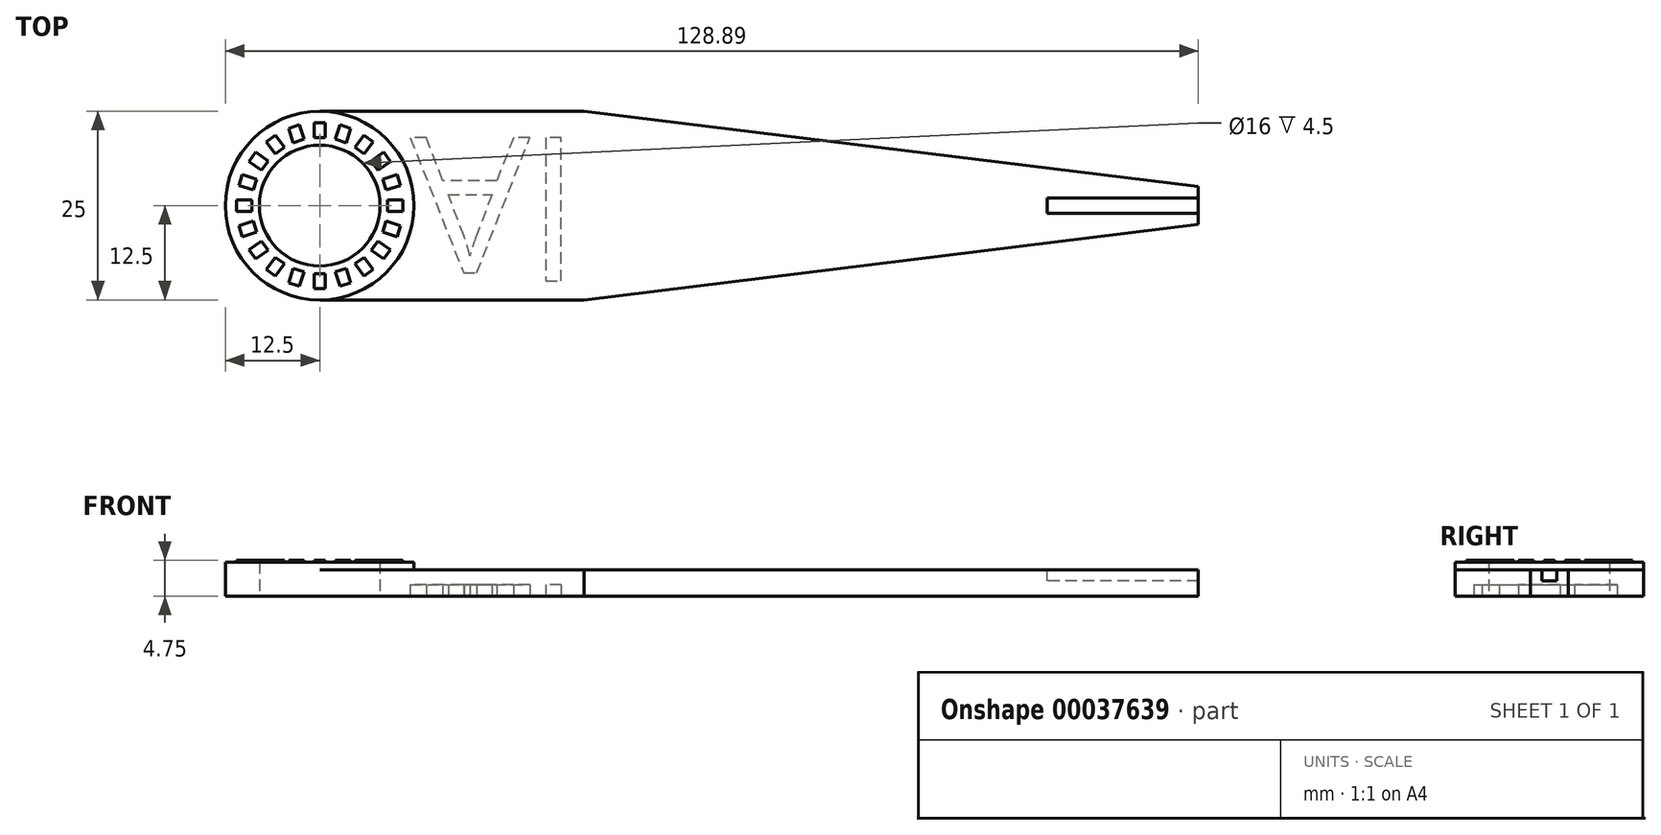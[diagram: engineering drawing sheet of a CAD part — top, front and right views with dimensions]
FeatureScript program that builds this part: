
annotation { "Feature Type Name" : "Feature", "Feature Type Description" : "" }
export const myFeature = defineFeature(function(context is Context, id is Id, definition is map)
    precondition{}
    {
        {
            var Q0;
            Q0=qCreatedBy(makeId("Top.planeOp"),FACE);
            var sketch = newSketch(context, id + "F0", { "sketchPlane" : qUnion([Q0])});
            skCircle(sketch, "E0", {"center": v(0, 0) * mm, "radius": 8 * mm});
            skCircle(sketch, "E1", {"center": v(0, 0) * mm, "radius": 12.5 * mm});
            skLineSegment(sketch, "E2", {"start": v(0, 12.5) * mm, "end": v(35, 12.5) * mm});
            skPoint(sketch, "E3", {"position": v(0, 12.5) * mm});
            skLineSegment(sketch, "E4", {"start": v(35, 12.5) * mm, "end": v(64.7, 12.5) * mm, "construction": true});
            skLineSegment(sketch, "E5", {"start": v(35, 12.5) * mm, "end": v(116.39, 2.5) * mm});
            skLineSegment(sketch, "E6", {"start": v(0, 0) * mm, "end": v(42.98, 0) * mm, "construction": true});
            skLineSegment(sketch, "E7.MirrorCS", {"start": v(35, -12.5) * mm, "end": v(116.39, -2.5) * mm});
            skLineSegment(sketch, "E8", {"start": v(116.39, 2.5) * mm, "end": v(116.39, -2.5) * mm});
            skLineSegment(sketch, "E9.MirrorCS", {"start": v(0, -12.5) * mm, "end": v(35, -12.5) * mm});
            skSolve(sketch);
        }
        {
            var Q0;
            Q0 = qSketchRegion(id + "F0", true);
            extrude(context, id + "F1", {"entities" : qUnion([Q0]), "depth" : 3.5 * mm});
        }
        {
            var Q0;
            Q0=makeQuery(id+"F1.opExtrude","CAP_FACE",FACE,{"disambiguationData":[OSD([sQuery(id+"F0.wireOp",EDGE,"E0"),sQuery(id+"F0.wireOp",EDGE,"E1"),sQuery(id+"F0.wireOp",EDGE,"E2"),sQuery(id+"F0.wireOp",EDGE,"E5"),sQuery(id+"F0.wireOp",EDGE,"E7.MirrorCS"),sQuery(id+"F0.wireOp",EDGE,"E8"),sQuery(id+"F0.wireOp",EDGE,"E9.MirrorCS")])],"isStart":false});
            var sketch = newSketch(context, id + "F2", { "sketchPlane" : qUnion([Q0])});
            skCircle(sketch, "E10", {"center": v(0, 0) * mm, "radius": 8 * mm});
            skCircle(sketch, "E11", {"center": v(0, 0) * mm, "radius": 12.5 * mm});
            skSolve(sketch);
        }
        {
            var Q0;
            Q0 = qSketchRegion(id + "F2", true);
            extrude(context, id + "F3", {"entities" : qUnion([Q0]), "operationType" : NewBodyOperationType.ADD, "depth" : 1 * mm});
        }
        {
            var Q0;
            Q0=makeQuery(id+"F3.opExtrude","CAP_FACE",FACE,{"disambiguationData":[OSD([sQuery(id+"F2.wireOp",EDGE,"E10"),sQuery(id+"F2.wireOp",EDGE,"E11")])],"isStart":false});
            var sketch = newSketch(context, id + "F4", { "sketchPlane" : qUnion([Q0])});
            skLineSegment(sketch, "E12.bottom", {"start": v(-0.75, 11) * mm, "end": v(0.75, 11) * mm});
            skLineSegment(sketch, "E12.top", {"start": v(-0.75, 9) * mm, "end": v(0.75, 9) * mm});
            skLineSegment(sketch, "E12.left", {"start": v(-0.75, 11) * mm, "end": v(-0.75, 9) * mm});
            skLineSegment(sketch, "E12.right", {"start": v(0.75, 11) * mm, "end": v(0.75, 9) * mm});
            skPoint(sketch, "E13", {"position": v(0, 8) * mm});
            skLineSegment(sketch, "E14.1.0", {"start": v(-4.11, 10.23) * mm, "end": v(-2.69, 10.7) * mm});
            skLineSegment(sketch, "E14.1.1", {"start": v(-4.11, 10.23) * mm, "end": v(-3.5, 8.33) * mm});
            skLineSegment(sketch, "E14.1.2", {"start": v(-3.5, 8.33) * mm, "end": v(-2.07, 8.8) * mm});
            skLineSegment(sketch, "E14.1.3", {"start": v(-2.69, 10.7) * mm, "end": v(-2.07, 8.8) * mm});
            skLineSegment(sketch, "E14.2.0", {"start": v(-7.07, 8.46) * mm, "end": v(-5.86, 9.34) * mm});
            skLineSegment(sketch, "E14.2.1", {"start": v(-7.07, 8.46) * mm, "end": v(-5.9, 6.84) * mm});
            skLineSegment(sketch, "E14.2.2", {"start": v(-5.9, 6.84) * mm, "end": v(-4.68, 7.72) * mm});
            skLineSegment(sketch, "E14.2.3", {"start": v(-5.86, 9.34) * mm, "end": v(-4.68, 7.72) * mm});
            skLineSegment(sketch, "E14.3.0", {"start": v(-9.34, 5.86) * mm, "end": v(-8.46, 7.07) * mm});
            skLineSegment(sketch, "E14.3.1", {"start": v(-9.34, 5.86) * mm, "end": v(-7.72, 4.68) * mm});
            skLineSegment(sketch, "E14.3.2", {"start": v(-7.72, 4.68) * mm, "end": v(-6.84, 5.9) * mm});
            skLineSegment(sketch, "E14.3.3", {"start": v(-8.46, 7.07) * mm, "end": v(-6.84, 5.9) * mm});
            skLineSegment(sketch, "E14.4.0", {"start": v(-10.7, 2.69) * mm, "end": v(-10.23, 4.11) * mm});
            skLineSegment(sketch, "E14.4.1", {"start": v(-10.7, 2.69) * mm, "end": v(-8.8, 2.07) * mm});
            skLineSegment(sketch, "E14.4.2", {"start": v(-8.8, 2.07) * mm, "end": v(-8.33, 3.5) * mm});
            skLineSegment(sketch, "E14.4.3", {"start": v(-10.23, 4.11) * mm, "end": v(-8.33, 3.5) * mm});
            skLineSegment(sketch, "E14.5.0", {"start": v(-11, -0.75) * mm, "end": v(-11, 0.75) * mm});
            skLineSegment(sketch, "E14.5.1", {"start": v(-11, -0.75) * mm, "end": v(-9, -0.75) * mm});
            skLineSegment(sketch, "E14.5.2", {"start": v(-9, -0.75) * mm, "end": v(-9, 0.75) * mm});
            skLineSegment(sketch, "E14.5.3", {"start": v(-11, 0.75) * mm, "end": v(-9, 0.75) * mm});
            skLineSegment(sketch, "E14.6.0", {"start": v(-10.23, -4.11) * mm, "end": v(-10.7, -2.69) * mm});
            skLineSegment(sketch, "E14.6.1", {"start": v(-10.23, -4.11) * mm, "end": v(-8.33, -3.5) * mm});
            skLineSegment(sketch, "E14.6.2", {"start": v(-8.33, -3.5) * mm, "end": v(-8.8, -2.07) * mm});
            skLineSegment(sketch, "E14.6.3", {"start": v(-10.7, -2.69) * mm, "end": v(-8.8, -2.07) * mm});
            skLineSegment(sketch, "E14.7.0", {"start": v(-8.46, -7.07) * mm, "end": v(-9.34, -5.86) * mm});
            skLineSegment(sketch, "E14.7.1", {"start": v(-8.46, -7.07) * mm, "end": v(-6.84, -5.9) * mm});
            skLineSegment(sketch, "E14.7.2", {"start": v(-6.84, -5.9) * mm, "end": v(-7.72, -4.68) * mm});
            skLineSegment(sketch, "E14.7.3", {"start": v(-9.34, -5.86) * mm, "end": v(-7.72, -4.68) * mm});
            skLineSegment(sketch, "E14.8.0", {"start": v(-5.86, -9.34) * mm, "end": v(-7.07, -8.46) * mm});
            skLineSegment(sketch, "E14.8.1", {"start": v(-5.86, -9.34) * mm, "end": v(-4.68, -7.72) * mm});
            skLineSegment(sketch, "E14.8.2", {"start": v(-4.68, -7.72) * mm, "end": v(-5.9, -6.84) * mm});
            skLineSegment(sketch, "E14.8.3", {"start": v(-7.07, -8.46) * mm, "end": v(-5.9, -6.84) * mm});
            skLineSegment(sketch, "E14.9.0", {"start": v(-2.69, -10.7) * mm, "end": v(-4.11, -10.23) * mm});
            skLineSegment(sketch, "E14.9.1", {"start": v(-2.69, -10.7) * mm, "end": v(-2.07, -8.8) * mm});
            skLineSegment(sketch, "E14.9.2", {"start": v(-2.07, -8.8) * mm, "end": v(-3.5, -8.33) * mm});
            skLineSegment(sketch, "E14.9.3", {"start": v(-4.11, -10.23) * mm, "end": v(-3.5, -8.33) * mm});
            skLineSegment(sketch, "E14.10.0", {"start": v(0.75, -11) * mm, "end": v(-0.75, -11) * mm});
            skLineSegment(sketch, "E14.10.1", {"start": v(0.75, -11) * mm, "end": v(0.75, -9) * mm});
            skLineSegment(sketch, "E14.10.2", {"start": v(0.75, -9) * mm, "end": v(-0.75, -9) * mm});
            skLineSegment(sketch, "E14.10.3", {"start": v(-0.75, -11) * mm, "end": v(-0.75, -9) * mm});
            skLineSegment(sketch, "E14.11.0", {"start": v(4.11, -10.23) * mm, "end": v(2.69, -10.7) * mm});
            skLineSegment(sketch, "E14.11.1", {"start": v(4.11, -10.23) * mm, "end": v(3.5, -8.33) * mm});
            skLineSegment(sketch, "E14.11.2", {"start": v(3.5, -8.33) * mm, "end": v(2.07, -8.8) * mm});
            skLineSegment(sketch, "E14.11.3", {"start": v(2.69, -10.7) * mm, "end": v(2.07, -8.8) * mm});
            skLineSegment(sketch, "E14.12.0", {"start": v(7.07, -8.46) * mm, "end": v(5.86, -9.34) * mm});
            skLineSegment(sketch, "E14.12.1", {"start": v(7.07, -8.46) * mm, "end": v(5.9, -6.84) * mm});
            skLineSegment(sketch, "E14.12.2", {"start": v(5.9, -6.84) * mm, "end": v(4.68, -7.72) * mm});
            skLineSegment(sketch, "E14.12.3", {"start": v(5.86, -9.34) * mm, "end": v(4.68, -7.72) * mm});
            skLineSegment(sketch, "E14.13.0", {"start": v(9.34, -5.86) * mm, "end": v(8.46, -7.07) * mm});
            skLineSegment(sketch, "E14.13.1", {"start": v(9.34, -5.86) * mm, "end": v(7.72, -4.68) * mm});
            skLineSegment(sketch, "E14.13.2", {"start": v(7.72, -4.68) * mm, "end": v(6.84, -5.9) * mm});
            skLineSegment(sketch, "E14.13.3", {"start": v(8.46, -7.07) * mm, "end": v(6.84, -5.9) * mm});
            skLineSegment(sketch, "E14.14.0", {"start": v(10.7, -2.69) * mm, "end": v(10.23, -4.11) * mm});
            skLineSegment(sketch, "E14.14.1", {"start": v(10.7, -2.69) * mm, "end": v(8.8, -2.07) * mm});
            skLineSegment(sketch, "E14.14.2", {"start": v(8.8, -2.07) * mm, "end": v(8.33, -3.5) * mm});
            skLineSegment(sketch, "E14.14.3", {"start": v(10.23, -4.11) * mm, "end": v(8.33, -3.5) * mm});
            skLineSegment(sketch, "E14.15.0", {"start": v(11, 0.75) * mm, "end": v(11, -0.75) * mm});
            skLineSegment(sketch, "E14.15.1", {"start": v(11, 0.75) * mm, "end": v(9, 0.75) * mm});
            skLineSegment(sketch, "E14.15.2", {"start": v(9, 0.75) * mm, "end": v(9, -0.75) * mm});
            skLineSegment(sketch, "E14.15.3", {"start": v(11, -0.75) * mm, "end": v(9, -0.75) * mm});
            skLineSegment(sketch, "E14.16.0", {"start": v(10.23, 4.11) * mm, "end": v(10.7, 2.69) * mm});
            skLineSegment(sketch, "E14.16.1", {"start": v(10.23, 4.11) * mm, "end": v(8.33, 3.5) * mm});
            skLineSegment(sketch, "E14.16.2", {"start": v(8.33, 3.5) * mm, "end": v(8.8, 2.07) * mm});
            skLineSegment(sketch, "E14.16.3", {"start": v(10.7, 2.69) * mm, "end": v(8.8, 2.07) * mm});
            skLineSegment(sketch, "E14.17.0", {"start": v(8.46, 7.07) * mm, "end": v(9.34, 5.86) * mm});
            skLineSegment(sketch, "E14.17.1", {"start": v(8.46, 7.07) * mm, "end": v(6.84, 5.9) * mm});
            skLineSegment(sketch, "E14.17.2", {"start": v(6.84, 5.9) * mm, "end": v(7.72, 4.68) * mm});
            skLineSegment(sketch, "E14.17.3", {"start": v(9.34, 5.86) * mm, "end": v(7.72, 4.68) * mm});
            skLineSegment(sketch, "E14.18.0", {"start": v(5.86, 9.34) * mm, "end": v(7.07, 8.46) * mm});
            skLineSegment(sketch, "E14.18.1", {"start": v(5.86, 9.34) * mm, "end": v(4.68, 7.72) * mm});
            skLineSegment(sketch, "E14.18.2", {"start": v(4.68, 7.72) * mm, "end": v(5.9, 6.84) * mm});
            skLineSegment(sketch, "E14.18.3", {"start": v(7.07, 8.46) * mm, "end": v(5.9, 6.84) * mm});
            skLineSegment(sketch, "E14.19.0", {"start": v(2.69, 10.7) * mm, "end": v(4.11, 10.23) * mm});
            skLineSegment(sketch, "E14.19.1", {"start": v(2.69, 10.7) * mm, "end": v(2.07, 8.8) * mm});
            skLineSegment(sketch, "E14.19.2", {"start": v(2.07, 8.8) * mm, "end": v(3.5, 8.33) * mm});
            skLineSegment(sketch, "E14.19.3", {"start": v(4.11, 10.23) * mm, "end": v(3.5, 8.33) * mm});
            skPoint(sketch, "E14.center", {"position": v(0, 0) * mm});
            skSolve(sketch);
        }
        {
            var Q0;
            Q0 = qSketchRegion(id + "F4", true);
            extrude(context, id + "F5", {"entities" : qUnion([Q0]), "operationType" : NewBodyOperationType.ADD, "depth" : .25 * mm});
        }
        {
            var Q0;
            Q0=makeQuery(id+"F1.opExtrude","CAP_FACE",FACE,{"disambiguationData":[OSD([sQuery(id+"F0.wireOp",EDGE,"E0"),sQuery(id+"F0.wireOp",EDGE,"E1"),sQuery(id+"F0.wireOp",EDGE,"E2"),sQuery(id+"F0.wireOp",EDGE,"E5"),sQuery(id+"F0.wireOp",EDGE,"E7.MirrorCS"),sQuery(id+"F0.wireOp",EDGE,"E8"),sQuery(id+"F0.wireOp",EDGE,"E9.MirrorCS")])],"isStart":false});
            var sketch = newSketch(context, id + "F6", { "sketchPlane" : qUnion([Q0])});
            skLineSegment(sketch, "E15.bottom", {"start": v(116.39, 1) * mm, "end": v(96.39, 1) * mm});
            skLineSegment(sketch, "E15.top", {"start": v(116.39, -1) * mm, "end": v(96.39, -1) * mm});
            skLineSegment(sketch, "E15.left", {"start": v(116.39, 1) * mm, "end": v(116.39, -1) * mm});
            skLineSegment(sketch, "E15.right", {"start": v(96.39, 1) * mm, "end": v(96.39, -1) * mm});
            skSolve(sketch);
        }
        {
            var Q0;
            Q0 = qSketchRegion(id + "F6", true);
            extrude(context, id + "F7", {"entities" : qUnion([Q0]), "operationType" : NewBodyOperationType.REMOVE, "oppositeDirection" : true, "depth" : 1.5 * mm});
        }
        {
            var Q0;
            Q0=sQuery(id+"F0.wireOp",EDGE,"E2");
            cPlane(context, id + "F8", {"entities" : qUnion([Q0]), "cplaneType" : CPlaneType.LINE_ANGLE, "offset" : 150 * mm, "angle" : 270 * degree, "width" : 150 * mm, "height" : 150 * mm});
        }
        {
            var Q0;
            Q0=qCreatedBy(id+"F8.planeOp",FACE);
            var sketch = newSketch(context, id + "F9", { "sketchPlane" : qUnion([Q0])});
            skText(sketch, "E16", { "text": "Al", "fontName": "OpenSans-Regular.ttf"});
            skPoint(sketch, "E17", {"position": v(12, 0) * mm});
            const initialGuessF9  = {"E16": [0.012, -0.009, 1, 0, 0.018]};
            skSetInitialGuess(sketch, initialGuessF9);
            skSolve(sketch);
        }
        {
            var Q0;
            Q0 = qSketchRegion(id + "F9", true);
            extrude(context, id + "F10", {"entities" : qUnion([Q0]), "operationType" : NewBodyOperationType.REMOVE, "oppositeDirection" : true, "depth" : 1.5 * mm});
        }
    });
